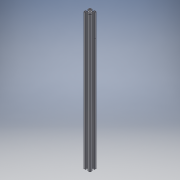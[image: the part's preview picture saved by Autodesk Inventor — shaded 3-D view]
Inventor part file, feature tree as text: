
AUTODESK INVENTOR PART (.ipt)
format: ipt  version: 2019 (Build 230136000, 136)  size: 342,016 bytes
history: native  units: in
note: dims shown in document units (in); Inventor stores cm internally (conversion verified against a paired STEP export)
features: extrude x1, sketch x1, projected_geometry x1
ambient origin geometry x8: Origin, YZ Plane, XZ Plane, XY Plane, X Axis, Y Axis, Z Axis, Center Point
bodies: Solid1 (feature_tree), Body1 (feature_tree)
feature tree (3):
  extrude  "Extrusion1"  [1 undecoded]
  sketch  "Sketch1"  dims[d0=15.748in d1=0.0in]
  projected_geometry  "Projected Loop1"
note: 1 required parameter value undecoded (feature->parameter linkage not recoverable at this tier; creation-order binding heuristic only, values carry confidence <= 0.55)
